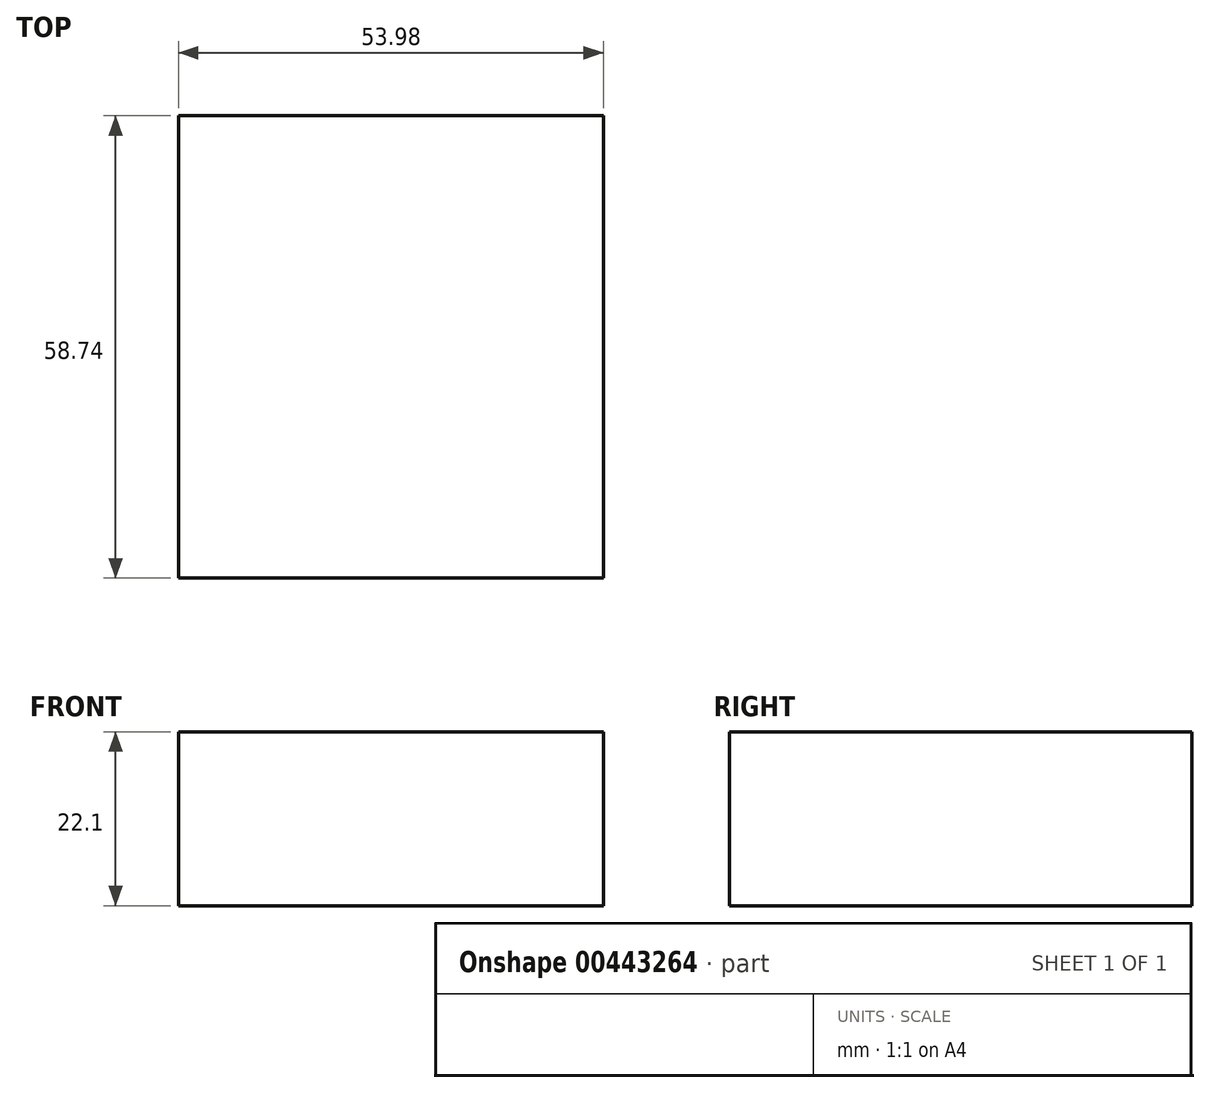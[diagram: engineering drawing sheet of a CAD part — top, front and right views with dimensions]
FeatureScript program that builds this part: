
annotation { "Feature Type Name" : "Feature", "Feature Type Description" : "" }
export const myFeature = defineFeature(function(context is Context, id is Id, definition is map)
    precondition{}
    {
        {
            var Q0;
            Q0=qCreatedBy(makeId("Top.planeOp"),FACE);
            var sketch = newSketch(context, id + "F0", { "sketchPlane" : qUnion([Q0])});
            skLineSegment(sketch, "E0.bottom", {"start": v(0, 0) * mm, "end": v(53.98, 0) * mm});
            skLineSegment(sketch, "E0.top", {"start": v(0, 58.74) * mm, "end": v(53.97, 58.74) * mm});
            skLineSegment(sketch, "E0.left", {"start": v(0, 0) * mm, "end": v(0, 58.74) * mm});
            skLineSegment(sketch, "E0.right", {"start": v(53.98, 0) * mm, "end": v(53.97, 58.74) * mm});
            skSolve(sketch);
        }
        {
            var Q0;
            Q0=makeQuery(id+"F0.imprint","IMPRINT",FACE,{"disambiguationData":[TD([[makeQuery(id+"F0.imprint","IMPRINT",EDGE,{"derivedFrom":sQuery(id+"F0.wireOp",EDGE,"E0.bottom")}),1.0]])]});
            extrude(context, id + "F1", {"entities" : qUnion([Q0]), "depth" : 22.1 * mm});
        }
    });
